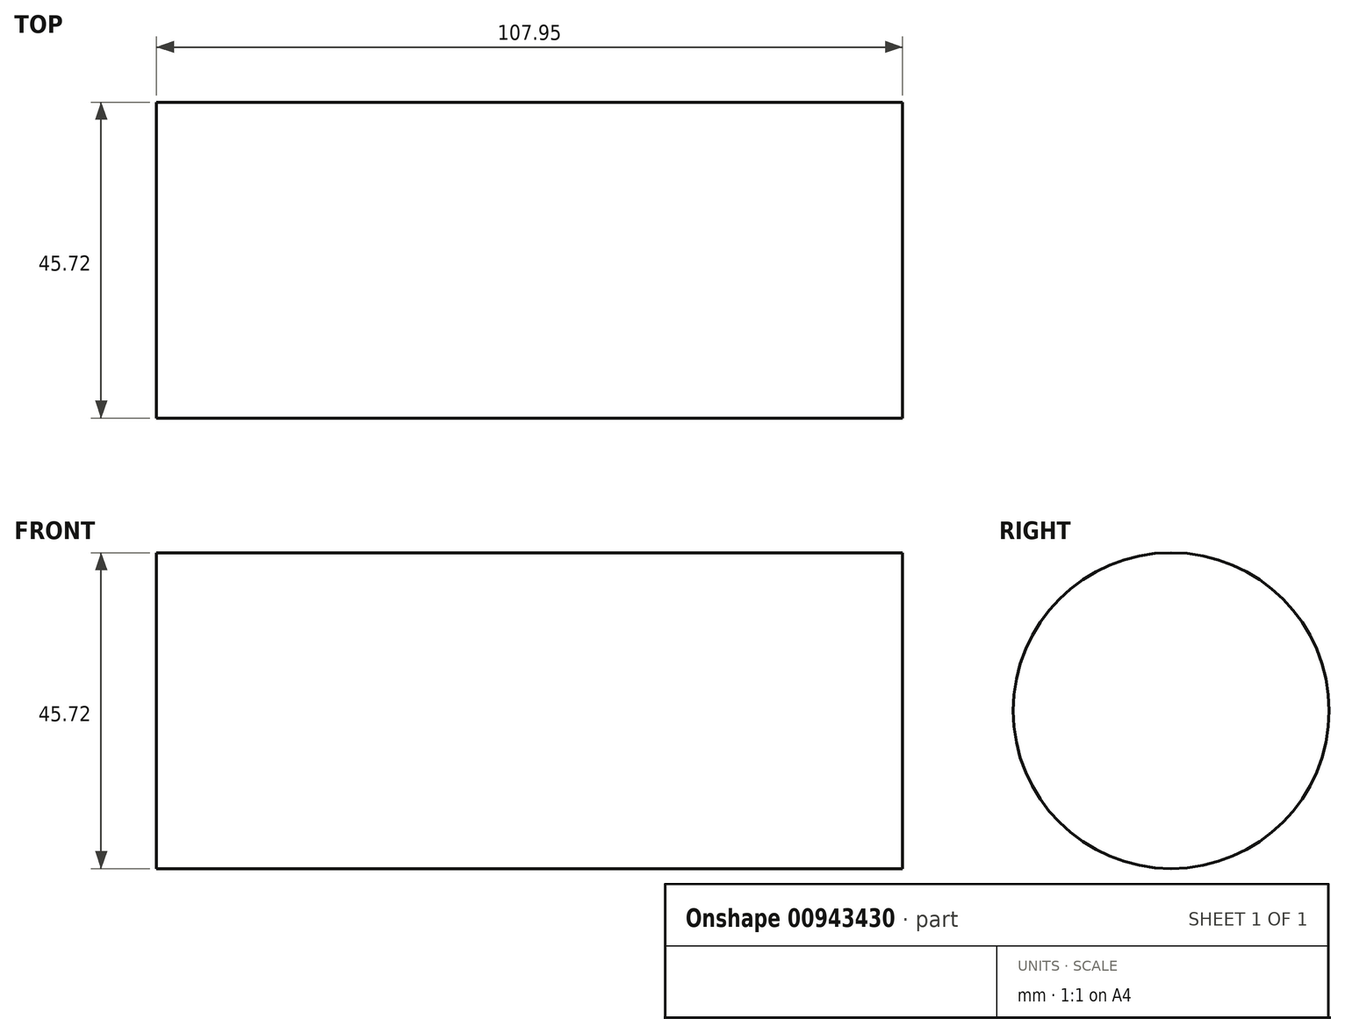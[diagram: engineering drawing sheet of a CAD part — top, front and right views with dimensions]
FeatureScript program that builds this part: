
annotation { "Feature Type Name" : "Feature", "Feature Type Description" : "" }
export const myFeature = defineFeature(function(context is Context, id is Id, definition is map)
    precondition{}
    {
        {
            var Q0;
            Q0=qCreatedBy(makeId("Right.planeOp"),FACE);
            var sketch = newSketch(context, id + "F0", { "sketchPlane" : qUnion([Q0])});
            skCircle(sketch, "E0", {"center": v(0, 0) * mm, "radius": 22.86 * mm});
            skSolve(sketch);
        }
        {
            var Q0;
            Q0=makeQuery(id+"F0.imprint","IMPRINT",FACE,{"disambiguationData":[TD([[makeQuery(id+"F0.imprint","IMPRINT",EDGE,{"derivedFrom":sQuery(id+"F0.wireOp",EDGE,"E0")}),1.0]])]});
            extrude(context, id + "F1", {"entities" : qUnion([Q0]), "depth" : 107.95 * mm, "offsetDistance" : 25.4 * mm});
        }
    });
